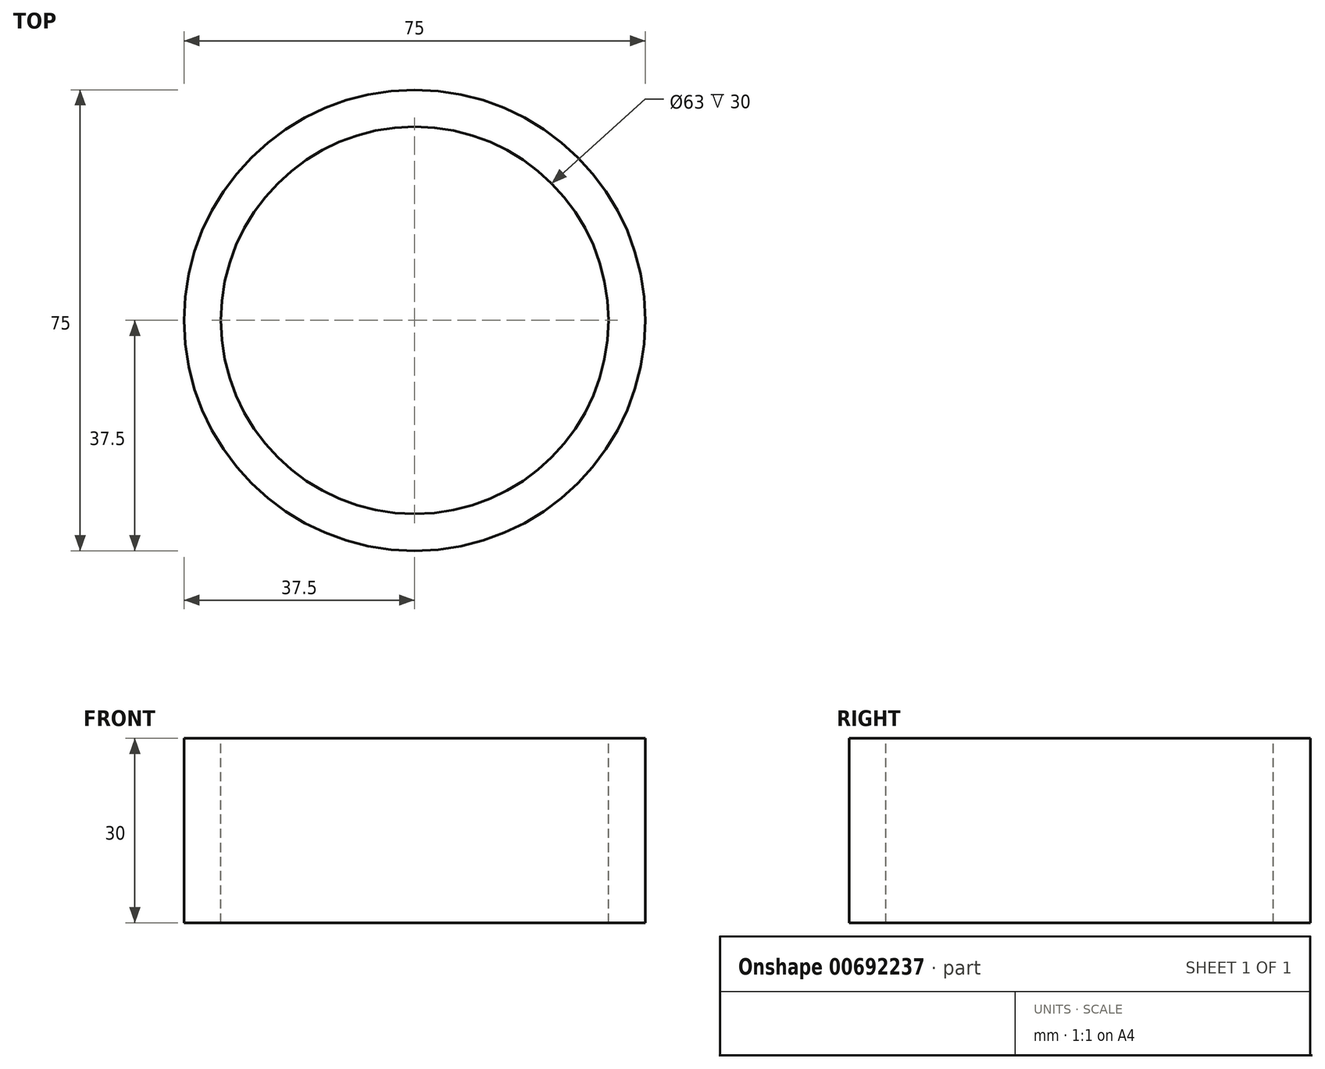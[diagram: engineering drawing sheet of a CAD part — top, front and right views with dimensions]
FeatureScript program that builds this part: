
annotation { "Feature Type Name" : "Feature", "Feature Type Description" : "" }
export const myFeature = defineFeature(function(context is Context, id is Id, definition is map)
    precondition{}
    {
        {
            var Q0;
            Q0=qCreatedBy(makeId("Front.planeOp"),FACE);
            var sketch = newSketch(context, id + "F0", { "sketchPlane" : qUnion([Q0])});
            skLineSegment(sketch, "E0", {"start": v(-37.5, 0) * mm, "end": v(-37.5, 30) * mm});
            skLineSegment(sketch, "E1", {"start": v(-37.5, 30) * mm, "end": v(-31.5, 30) * mm});
            skLineSegment(sketch, "E2", {"start": v(-31.5, 30) * mm, "end": v(-31.5, 0) * mm});
            skLineSegment(sketch, "E3", {"start": v(-31.5, 0) * mm, "end": v(-37.5, 0) * mm});
            skLineSegment(sketch, "E4", {"start": v(0, 0) * mm, "end": v(0, -22.46) * mm});
            skSolve(sketch);
        }
        {
            var Q0;
            Q0=makeQuery(id+"F0.imprint","IMPRINT",FACE,{"disambiguationData":[TD([[makeQuery(id+"F0.imprint","IMPRINT",EDGE,{"derivedFrom":sQuery(id+"F0.wireOp",EDGE,"E0")}),-1.0]])]});
            var Q1;
            Q1=sQuery(id+"F0.wireOp",EDGE,"E4");
            revolve(context, id + "F1", {"surfaceOperationType" : NewSurfaceOperationType.NEW, "entities" : qUnion([Q0]), "axis" : qUnion([Q1]), "revolveType" : RevolveType.FULL});
        }
    });
